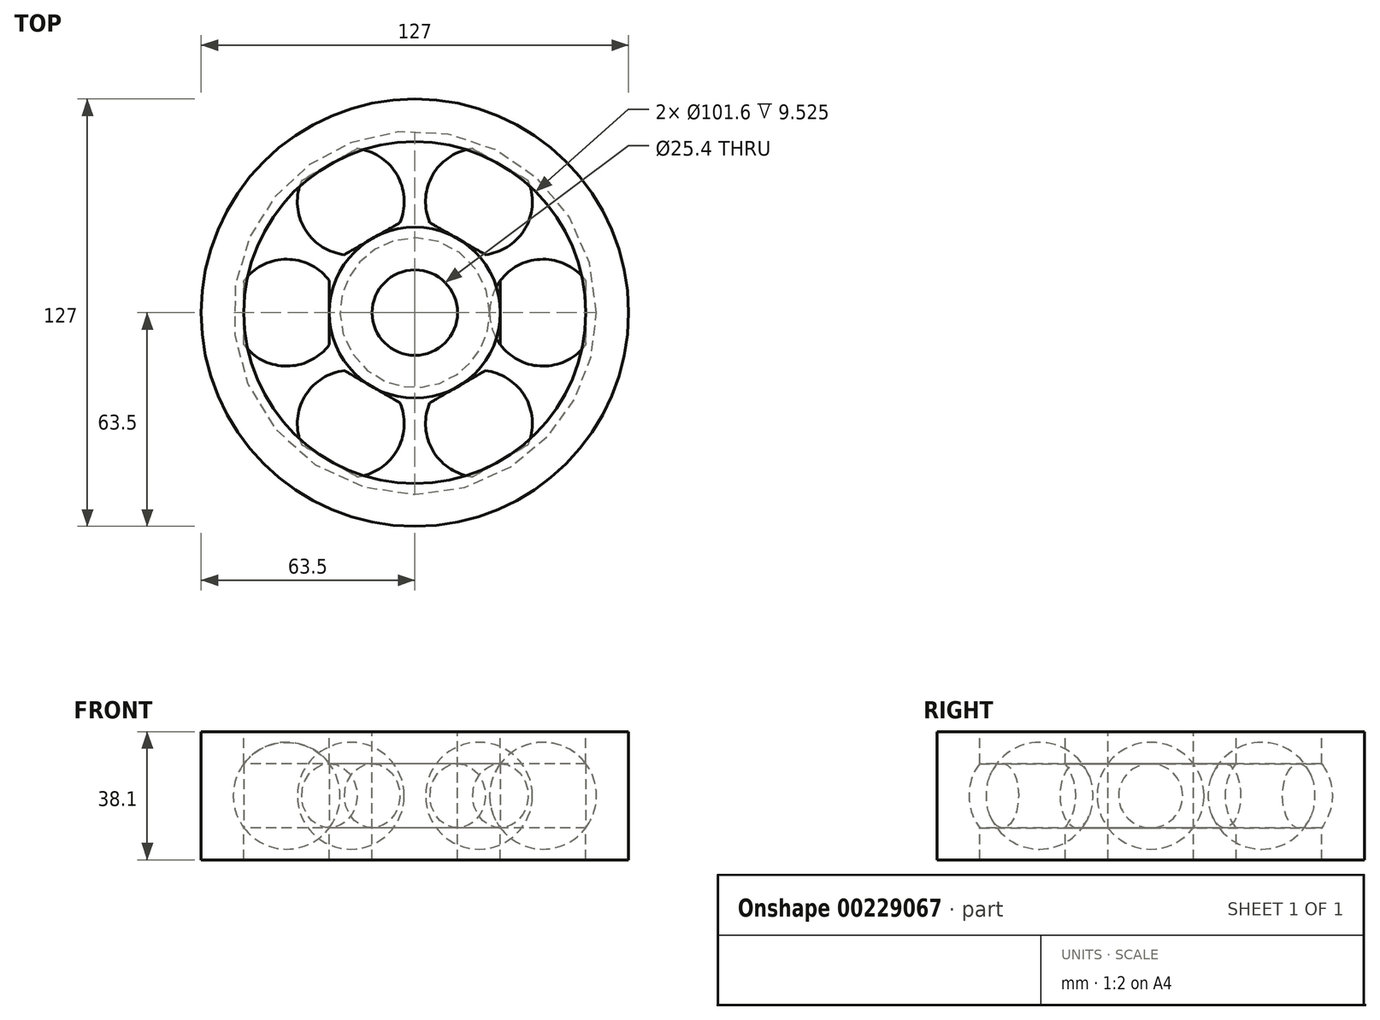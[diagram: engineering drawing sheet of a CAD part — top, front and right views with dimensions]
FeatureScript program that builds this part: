
annotation { "Feature Type Name" : "Feature", "Feature Type Description" : "" }
export const myFeature = defineFeature(function(context is Context, id is Id, definition is map)
    precondition{}
    {
        {
            var Q0;
            Q0=qCreatedBy(makeId("Front.planeOp"),FACE);
            var sketch = newSketch(context, id + "F0", { "sketchPlane" : qUnion([Q0])});
            skLineSegment(sketch, "E0", {"start": v(0, 19.05) * mm, "end": v(0, -19.05) * mm, "construction": true});
            skLineSegment(sketch, "E1", {"start": v(12.7, 19.05) * mm, "end": v(12.7, -19.05) * mm});
            skLineSegment(sketch, "E2", {"start": v(12.7, -19.05) * mm, "end": v(25.4, -19.05) * mm});
            skLineSegment(sketch, "E3", {"start": v(25.4, -19.05) * mm, "end": v(25.4, 19.05) * mm});
            skLineSegment(sketch, "E4", {"start": v(25.4, 19.05) * mm, "end": v(12.7, 19.05) * mm});
            skCircle(sketch, "E5", {"center": v(38.1, 0) * mm, "radius": 15.88 * mm});
            skLineSegment(sketch, "E6.bottom", {"start": v(50.8, 19.05) * mm, "end": v(63.5, 19.05) * mm});
            skLineSegment(sketch, "E6.top", {"start": v(50.8, -19.05) * mm, "end": v(63.5, -19.05) * mm});
            skLineSegment(sketch, "E6.left", {"start": v(50.8, 19.05) * mm, "end": v(50.8, -19.05) * mm});
            skLineSegment(sketch, "E6.right", {"start": v(63.5, 19.05) * mm, "end": v(63.5, -19.05) * mm});
            skLineSegment(sketch, "E7", {"start": v(22.22, 0) * mm, "end": v(53.97, 0) * mm});
            skLineSegment(sketch, "E8", {"start": v(12.7, 0) * mm, "end": v(22.22, 0) * mm, "construction": true});
            skLineSegment(sketch, "E9", {"start": v(53.97, 0) * mm, "end": v(63.5, 0) * mm, "construction": true});
            skSolve(sketch);
        }
        {
            var Q0;
            Q0=makeQuery(id+"F0.imprint","IMPRINT",FACE,{"disambiguationData":[TD([[makeQuery(id+"F0.imprint","IMPRINT",EDGE,{"derivedFrom":sQuery(id+"F0.wireOp",EDGE,"E1")}),1.0]])]});
            var Q1;
            {var subQ6=sQuery(id+"F0.wireOp",EDGE,"E6.bottom");Q1=makeQuery(id+"F0.imprint","IMPRINT",FACE,{"disambiguationData":[TD([[makeQuery(id+"F0.imprint","IMPRINT",EDGE,{"derivedFrom":subQ6}),-1.0]])]});}
            var Q2;
            Q2=sQuery(id+"F0.wireOp",EDGE,"E0");
            revolve(context, id + "F1", {"entities" : qUnion([Q0, Q1]), "axis" : qUnion([Q2]), "revolveType" : RevolveType.FULL});
        }
        {
            var Q0;
            {var subQ0=sQuery(id+"F0.wireOp",EDGE,"E5");var subQ1=sQuery(id+"F0.wireOp",EDGE,"E3");var subQ2=makeQuery(id+"F0.imprint","INTERSECT",VERTEX,{"disambiguationData":[OD(0.0)],"derivedFrom":[subQ1,subQ0]});Q0=makeQuery(id+"F0.imprint","IMPRINT",FACE,{"disambiguationData":[TD([[makeQuery(id+"F0.imprint","IMPRINT",EDGE,{"disambiguationData":[TD([[subQ2,-1.0]])],"derivedFrom":subQ1}),1.0]])]});}
            var Q1;
            {var subQ0=sQuery(id+"F0.wireOp",EDGE,"E5");var subQ1=sQuery(id+"F0.wireOp",EDGE,"E3");var subQ2=makeQuery(id+"F0.imprint","INTERSECT",VERTEX,{"disambiguationData":[OD(1.0)],"derivedFrom":[subQ1,subQ0]});Q1=makeQuery(id+"F0.imprint","IMPRINT",FACE,{"disambiguationData":[TD([[makeQuery(id+"F0.imprint","IMPRINT",EDGE,{"disambiguationData":[TD([[subQ2,1.0]])],"derivedFrom":subQ1}),-1.0]])]});}
            var Q2;
            Q2=sQuery(id+"F0.wireOp",EDGE,"E7");
            revolve(context, id + "F2", {"operationType" : NewBodyOperationType.ADD, "entities" : qUnion([Q0, Q1]), "axis" : qUnion([Q2]), "revolveType" : RevolveType.FULL});
        }
        {
            var Q0;
            Q0=makeQuery(id+"F2.opRevolve","SWEPT_BODY",BODY,{"disambiguationData":[OSD([sQuery(id+"F0.wireOp",EDGE,"E3"),sQuery(id+"F0.wireOp",EDGE,"E5"),sQuery(id+"F0.wireOp",EDGE,"E6.left"),sQuery(id+"F0.wireOp",EDGE,"E7")])]});
            var Q1;
            Q1=sQuery(id+"F0.wireOp",EDGE,"E0");
            circularPattern(context, id + "F3", {"entities" : qUnion([Q0]), "axis" : qUnion([Q1]), "angle" : 360 * degree, "instanceCount" : 6, "equalSpace" : true});
        }
    });
